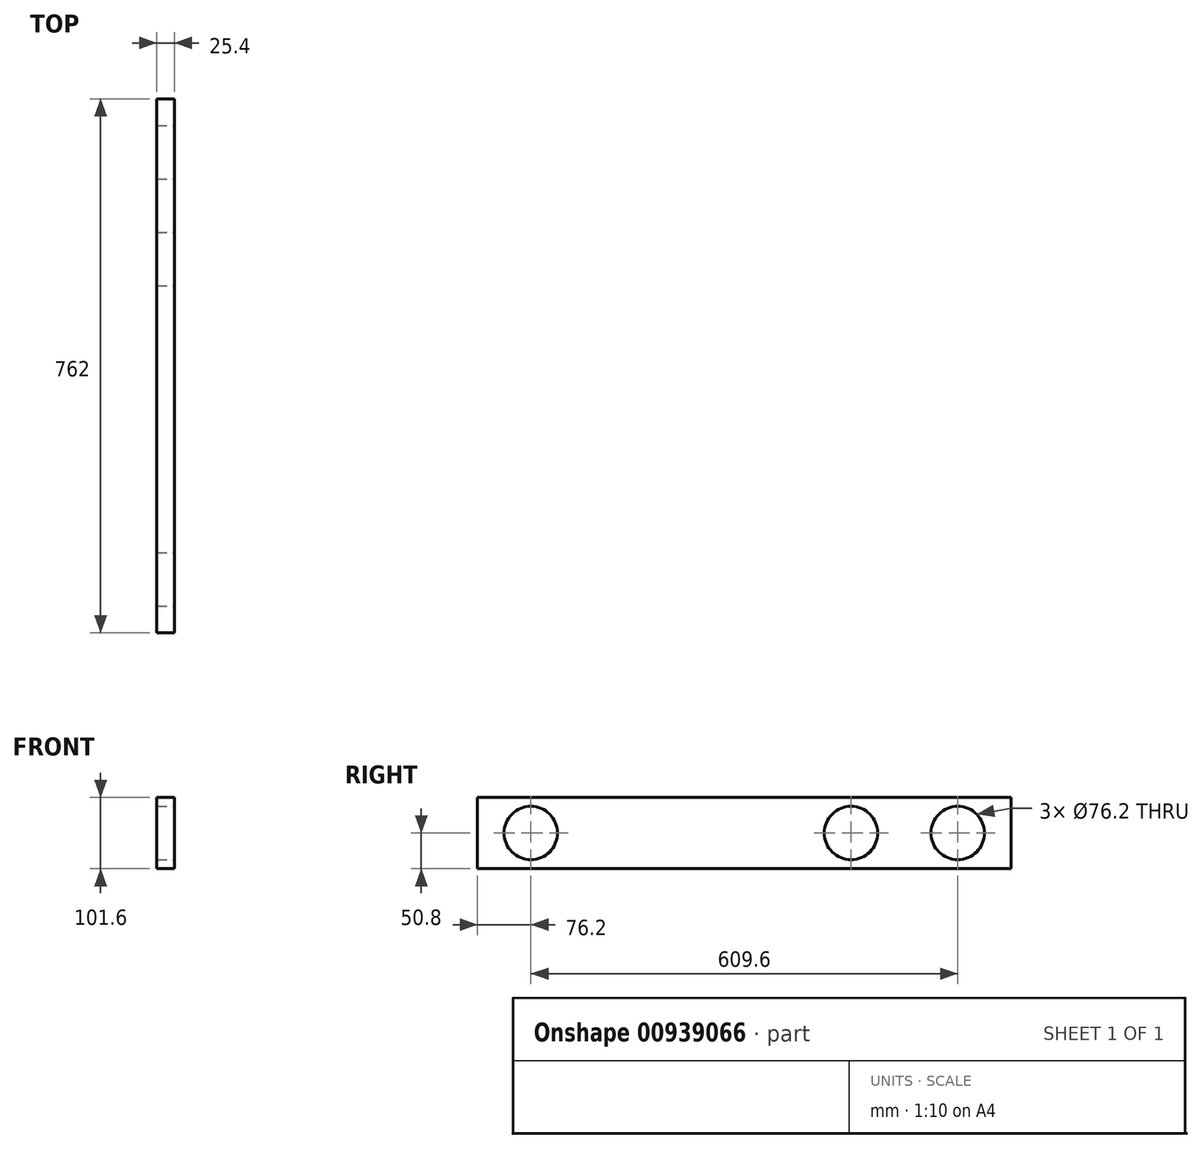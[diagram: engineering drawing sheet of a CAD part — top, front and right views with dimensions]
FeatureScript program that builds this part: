
annotation { "Feature Type Name" : "Feature", "Feature Type Description" : "" }
export const myFeature = defineFeature(function(context is Context, id is Id, definition is map)
    precondition{}
    {
        {
            var Q0;
            Q0=qCreatedBy(makeId("Right.planeOp"),FACE);
            var sketch = newSketch(context, id + "F0", { "sketchPlane" : qUnion([Q0])});
            skLineSegment(sketch, "E0.bottom", {"start": v(304.8, 50.8) * mm, "end": v(-304.8, 50.8) * mm});
            skLineSegment(sketch, "E0.top", {"start": v(304.8, -50.8) * mm, "end": v(-304.8, -50.8) * mm});
            skLineSegment(sketch, "E0.left", {"start": v(304.8, 50.8) * mm, "end": v(304.8, -50.8) * mm});
            skLineSegment(sketch, "E0.right", {"start": v(-304.8, 50.8) * mm, "end": v(-304.8, -50.8) * mm});
            skPoint(sketch, "E0.middle", {"position": v(0, 0) * mm});
            skSolve(sketch);
        }
        {
            var Q0;
            Q0 = qSketchRegion(id + "F0", true);
            extrude(context, id + "F1", {"entities" : qUnion([Q0]), "endBound" : BoundingType.SYMMETRIC, "depth" : 25.4 * mm, "offsetDistance" : 25.4 * mm});
        }
        {
            var Q0;
            Q0=makeQuery(id+"F1.opExtrude","CAP_FACE",FACE,{"disambiguationData":[OSD([sQuery(id+"F0.wireOp",EDGE,"E0.bottom"),sQuery(id+"F0.wireOp",EDGE,"E0.top"),sQuery(id+"F0.wireOp",EDGE,"E0.left"),sQuery(id+"F0.wireOp",EDGE,"E0.right")])],"isStart":false});
            var sketch = newSketch(context, id + "F2", { "sketchPlane" : qUnion([Q0])});
            skCircle(sketch, "E1", {"center": v(-228.6, 0) * mm, "radius": 38.1 * mm});
            skCircle(sketch, "E2.MirrorC", {"center": v(228.6, 0) * mm, "radius": 38.1 * mm});
            skSolve(sketch);
        }
        {
            var Q0;
            Q0 = qSketchRegion(id + "F2", true);
            extrude(context, id + "F3", {"entities" : qUnion([Q0]), "operationType" : NewBodyOperationType.REMOVE, "oppositeDirection" : true, "depth" : 25.4 * mm, "offsetDistance" : 25.4 * mm});
        }
        {
            var Q0;
            Q0=makeQuery(id+"F1.opExtrude","SWEPT_FACE",FACE,{"disambiguationData":[OSD([sQuery(id+"F0.wireOp",EDGE,"E0.left")])]});
            extrude(context, id + "F4", {"entities" : qUnion([Q0]), "operationType" : NewBodyOperationType.ADD, "depth" : 152.4 * mm, "offsetDistance" : 25.4 * mm});
        }
        {
            var Q0;
            {var subQ0=sQuery(id+"F0.wireOp",EDGE,"E0.left");Q0=makeQuery(id+"F4.boolean.opBoolean","MERGE",FACE,{"derivedFrom":[makeQuery(id+"F1.opExtrude","CAP_FACE",FACE,{"disambiguationData":[OSD([sQuery(id+"F0.wireOp",EDGE,"E0.bottom"),sQuery(id+"F0.wireOp",EDGE,"E0.top"),subQ0,sQuery(id+"F0.wireOp",EDGE,"E0.right")])],"isStart":false}),makeQuery(id+"F4.opExtrude","SWEPT_FACE",FACE,{"disambiguationData":[OSD([subQ0]),TDD([makeQuery(id+"F1.opExtrude","CAP_EDGE",EDGE,{"disambiguationData":[OSD([subQ0])],"isStart":false})])]})]});}
            var sketch = newSketch(context, id + "F5", { "sketchPlane" : qUnion([Q0])});
            skCircle(sketch, "E3", {"center": v(381, 0) * mm, "radius": 38.1 * mm});
            skSolve(sketch);
        }
        {
            var Q0;
            Q0 = qSketchRegion(id + "F5", true);
            extrude(context, id + "F6", {"entities" : qUnion([Q0]), "operationType" : NewBodyOperationType.REMOVE, "oppositeDirection" : true, "depth" : 25.4 * mm, "offsetDistance" : 25.4 * mm});
        }
    });
